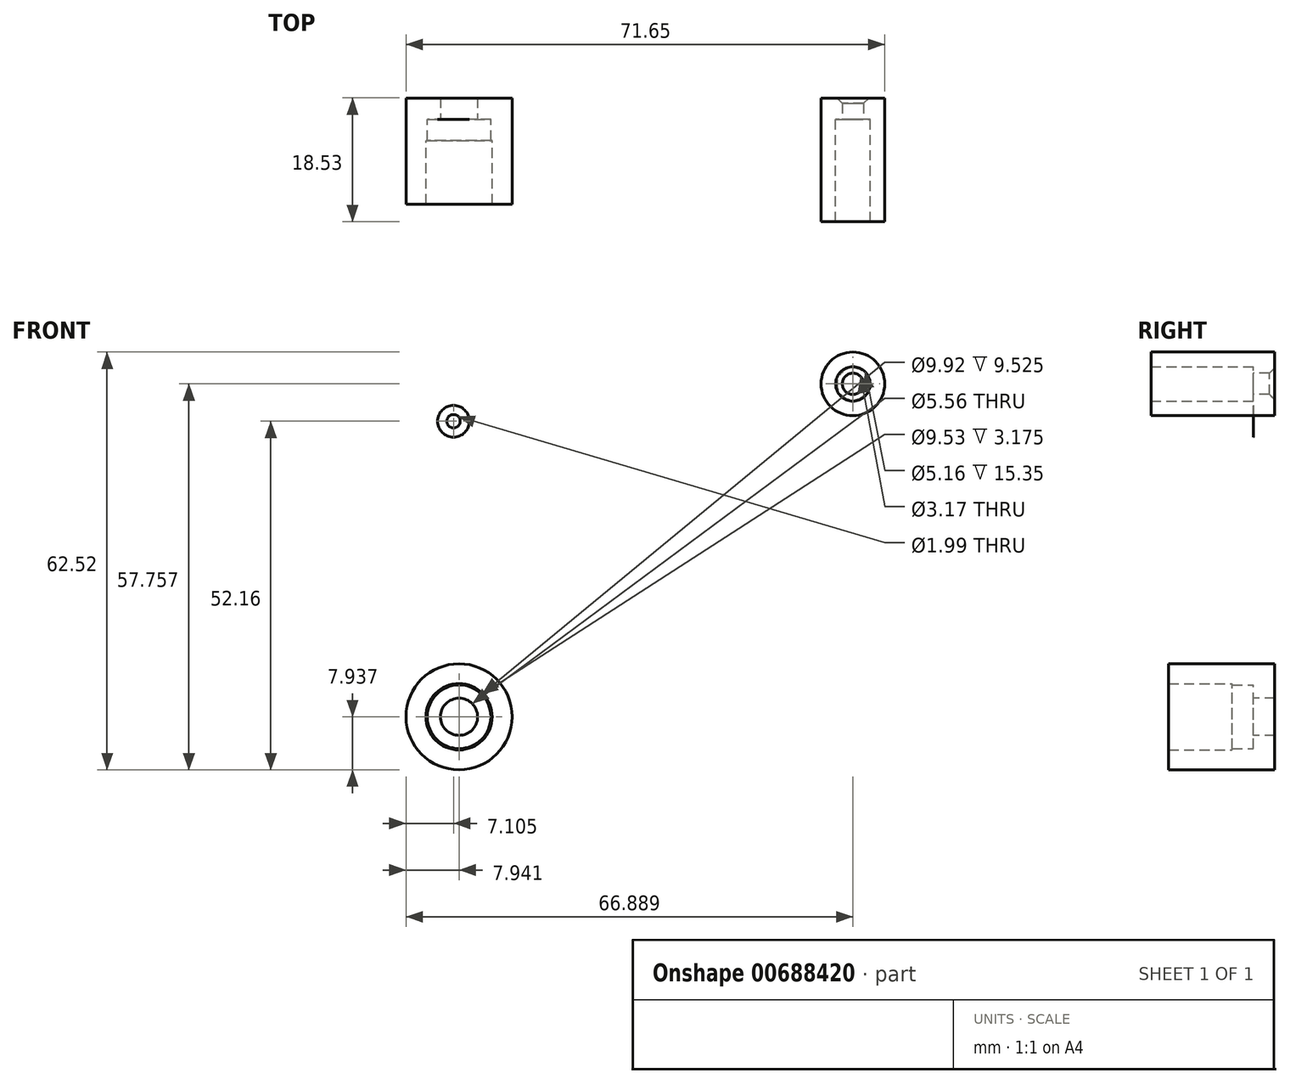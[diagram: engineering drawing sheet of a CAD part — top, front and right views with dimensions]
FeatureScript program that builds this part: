
annotation { "Feature Type Name" : "Feature", "Feature Type Description" : "" }
export const myFeature = defineFeature(function(context is Context, id is Id, definition is map)
    precondition{}
    {
        {
            var Q0;
            Q0=qCreatedBy(makeId("Front.planeOp"),FACE);
            var sketch = newSketch(context, id + "F0", { "sketchPlane" : qUnion([Q0])});
            skCircle(sketch, "E0", {"center": v(-39.3, 31.8) * mm, "radius": 2.38 * mm});
            skSolve(sketch);
        }
        {
            var Q0;
            Q0 = qSketchRegion(id + "F0", true);
            extrude(context, id + "F1", {"entities" : qUnion([Q0]), "depth" : 3 / 101.6 * mm, "offsetDistance" : 25.4 * mm});
        }
        {
            var Q0;
            Q0=qCreatedBy(makeId("Front.planeOp"),FACE);
            var sketch = newSketch(context, id + "F2", { "sketchPlane" : qUnion([Q0])});
            skCircle(sketch, "E1", {"center": v(20.48, 37.4) * mm, "radius": 4.76 * mm});
            skCircle(sketch, "E2", {"center": v(20.48, 37.4) * mm, "radius": 2.58 * mm});
            skCircle(sketch, "E3", {"center": v(20.48, 37.4) * mm, "radius": 1.59 * mm});
            skSolve(sketch);
        }
        {
            var Q0;
            Q0=makeQuery(id+"F2.imprint","IMPRINT",FACE,{"disambiguationData":[TD([[makeQuery(id+"F2.imprint","IMPRINT",EDGE,{"derivedFrom":sQuery(id+"F2.wireOp",EDGE,"E1")}),1.0]])]});
            extrude(context, id + "F3", {"entities" : qUnion([Q0]), "depth" : 15.35 * mm, "offsetDistance" : 25.4 * mm});
        }
        {
            var Q0;
            Q0=makeQuery(id+"F2.imprint","IMPRINT",FACE,{"disambiguationData":[TD([[makeQuery(id+"F2.imprint","IMPRINT",EDGE,{"derivedFrom":sQuery(id+"F2.wireOp",EDGE,"E2")}),1.0]])]});
            var Q1;
            Q1=makeQuery(id+"F2.imprint","IMPRINT",FACE,{"disambiguationData":[TD([[makeQuery(id+"F2.imprint","IMPRINT",EDGE,{"derivedFrom":sQuery(id+"F2.wireOp",EDGE,"E1")}),1.0]])]});
            extrude(context, id + "F4", {"entities" : qUnion([Q0, Q1]), "operationType" : NewBodyOperationType.ADD, "oppositeDirection" : true, "depth" : 3.17 * mm, "offsetDistance" : 25.4 * mm});
        }
        {
            var Q0;
            Q0=makeQuery(id+"F4.opExtrude","CAP_EDGE",EDGE,{"disambiguationData":[OSD([sQuery(id+"F2.wireOp",EDGE,"E3")])],"isStart":false});
            chamfer(context, id + "F5", {"entities" : qUnion([Q0]), "width" : 0.8 * mm, "tangentPropagation" : true});
        }
        {
            var Q0;
            Q0=qCreatedBy(makeId("Front.planeOp"),FACE);
            var sketch = newSketch(context, id + "F6", { "sketchPlane" : qUnion([Q0])});
            skCircle(sketch, "E4", {"center": v(-38.47, -12.42) * mm, "radius": 4.96 * mm});
            skCircle(sketch, "E5", {"center": v(-38.47, -12.42) * mm, "radius": 7.94 * mm});
            skCircle(sketch, "E6", {"center": v(-38.47, -12.42) * mm, "radius": 2.78 * mm});
            skCircle(sketch, "E7", {"center": v(-38.47, -12.42) * mm, "radius": 4.76 * mm});
            skSolve(sketch);
        }
        {
            var Q0;
            Q0=makeQuery(id+"F6.imprint","IMPRINT",FACE,{"disambiguationData":[TD([[makeQuery(id+"F6.imprint","IMPRINT",EDGE,{"derivedFrom":sQuery(id+"F6.wireOp",EDGE,"E4")}),-1.0]])]});
            extrude(context, id + "F7", {"entities" : qUnion([Q0]), "depth" : 12.7 * mm, "offsetDistance" : 25.4 * mm});
        }
        {
            var Q0;
            Q0=makeQuery(id+"F6.imprint","IMPRINT",FACE,{"disambiguationData":[TD([[makeQuery(id+"F6.imprint","IMPRINT",EDGE,{"derivedFrom":sQuery(id+"F6.wireOp",EDGE,"E4")}),1.0]])]});
            var Q1;
            Q1=makeQuery(id+"F6.imprint","IMPRINT",FACE,{"disambiguationData":[TD([[makeQuery(id+"F6.imprint","IMPRINT",EDGE,{"derivedFrom":sQuery(id+"F6.wireOp",EDGE,"E4")}),-1.0]])]});
            var Q2;
            Q2=makeQuery(id+"F6.imprint","IMPRINT",FACE,{"disambiguationData":[TD([[makeQuery(id+"F6.imprint","IMPRINT",EDGE,{"derivedFrom":sQuery(id+"F6.wireOp",EDGE,"E6")}),-1.0]])]});
            extrude(context, id + "F8", {"entities" : qUnion([Q0, Q1, Q2]), "operationType" : NewBodyOperationType.ADD, "oppositeDirection" : true, "depth" : 3.17 * mm, "offsetDistance" : 25.4 * mm});
        }
        {
            var Q0;
            Q0=makeQuery(id+"F6.imprint","IMPRINT",FACE,{"disambiguationData":[TD([[makeQuery(id+"F6.imprint","IMPRINT",EDGE,{"derivedFrom":sQuery(id+"F6.wireOp",EDGE,"E4")}),1.0]])]});
            extrude(context, id + "F9", {"entities" : qUnion([Q0]), "operationType" : NewBodyOperationType.ADD, "depth" : 3.17 * mm, "offsetDistance" : 25.4 * mm});
        }
        {
            var Q0;
            Q0=sQuery(id+"F0.wireOp",VERTEX,"E0.center");
            var Q1;
            Q1=makeQuery(id+"F1.opExtrude","SWEPT_BODY",BODY,{"disambiguationData":[OSD([sQuery(id+"F0.wireOp",EDGE,"E0")])]});
            hole(context, id + "F10", {"style" : HoleStyle.SIMPLE, "endStyle" : HoleEndStyle.BLIND, "oppositeDirection" : true, "standardTappedOrClearance" : lookupTablePath({ "standard" : "ANSI", "engagement" : "75%", "pitch" : "48 tpi", "size" : "#3", "type" : "Tapped" }), "standardBlindInLast" : lookupTablePath({ "standard" : "ANSI", "engagement" : "75%", "pitch" : "48 tpi", "size" : "#3", "type" : "Tapped" }), "holeDiameter" : 2 * mm, "majorDiameter" : 2.5 * mm, "showTappedDepth" : true, "holeDepth" : 3.17 * mm, "tappedDepth" : 1.59 * mm, "tapClearance" : 3, "locations" : qUnion([Q0]), "scope" : qUnion([Q1])});
        }
    });
